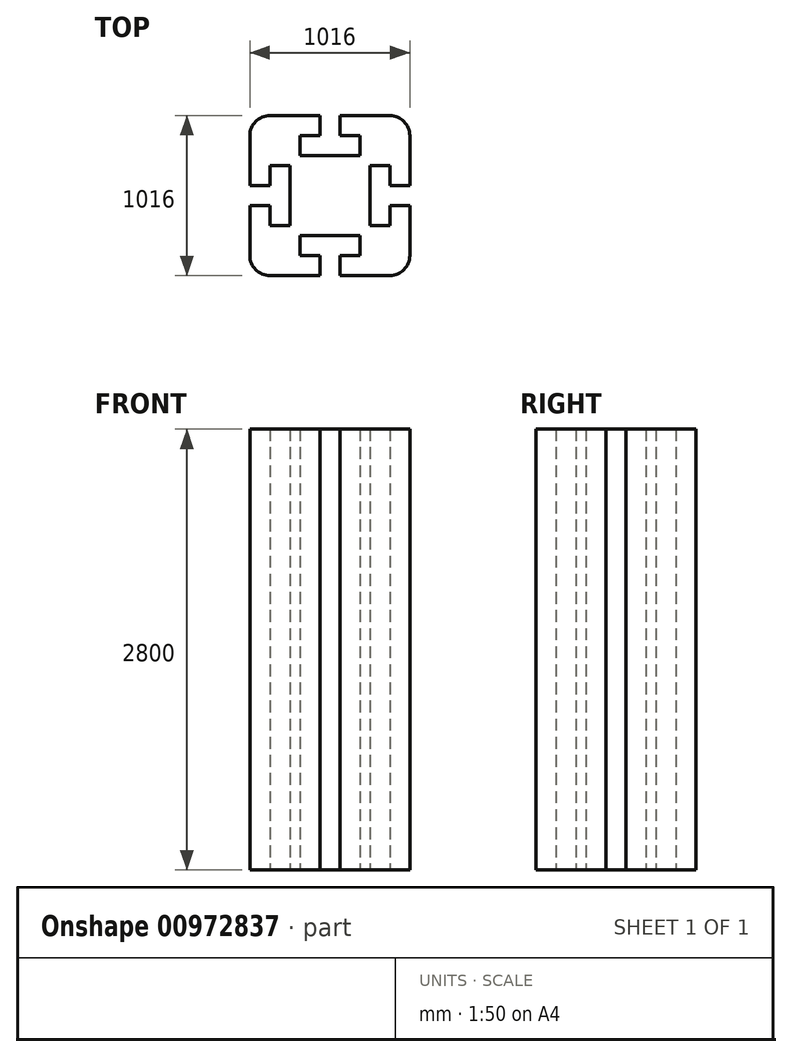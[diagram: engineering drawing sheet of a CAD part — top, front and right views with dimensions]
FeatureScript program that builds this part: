
annotation { "Feature Type Name" : "Feature", "Feature Type Description" : "" }
export const myFeature = defineFeature(function(context is Context, id is Id, definition is map)
    precondition{}
    {
        {
            var Q0;
            Q0=qCreatedBy(makeId("Top.planeOp"),FACE);
            var sketch = newSketch(context, id + "F0", { "sketchPlane" : qUnion([Q0])});
            skLineSegment(sketch, "E0.bottom", {"start": v(-381, 508) * mm, "end": v(-63.5, 508) * mm});
            skLineSegment(sketch, "E0.top", {"start": v(-381, -508) * mm, "end": v(-63.5, -508) * mm});
            skLineSegment(sketch, "E0.left", {"start": v(-508, 381) * mm, "end": v(-508, 63.5) * mm});
            skLineSegment(sketch, "E0.right", {"start": v(508, 381) * mm, "end": v(508, 63.5) * mm});
            skPoint(sketch, "E1.visualSharp", {"position": v(508, 508) * mm});
            skArc(sketch, "E1.filletArc", {"start": v(508, 381) * mm, "mid": v(470.8, 470.8) * mm, "end": v(381, 508) * mm});
            skPoint(sketch, "E2.visualSharp", {"position": v(-508, 508) * mm});
            skArc(sketch, "E2.filletArc", {"start": v(-381, 508) * mm, "mid": v(-470.8, 470.8) * mm, "end": v(-508, 381) * mm});
            skArc(sketch, "E3.filletArc", {"start": v(-508, -381) * mm, "mid": v(-470.8, -470.8) * mm, "end": v(-381, -508) * mm});
            skPoint(sketch, "E4.visualSharp", {"position": v(508, -508) * mm});
            skArc(sketch, "E4.filletArc", {"start": v(381, -508) * mm, "mid": v(470.8, -470.8) * mm, "end": v(508, -381) * mm});
            skLineSegment(sketch, "E5", {"start": v(508, 63.5) * mm, "end": v(381, 63.5) * mm});
            skLineSegment(sketch, "E6", {"start": v(381, 63.5) * mm, "end": v(381, 190.5) * mm});
            skLineSegment(sketch, "E7", {"start": v(381, 190.5) * mm, "end": v(254, 190.5) * mm});
            skLineSegment(sketch, "E8", {"start": v(254, 190.5) * mm, "end": v(254, -190.5) * mm});
            skLineSegment(sketch, "E9", {"start": v(254, -190.5) * mm, "end": v(381, -190.5) * mm});
            skLineSegment(sketch, "E10", {"start": v(381, -190.5) * mm, "end": v(381, -63.5) * mm});
            skLineSegment(sketch, "E11", {"start": v(381, -63.5) * mm, "end": v(508, -63.5) * mm});
            skLineSegment(sketch, "E12.trimOffspring", {"start": v(508, -63.5) * mm, "end": v(508, -381) * mm});
            skLineSegment(sketch, "E13", {"start": v(-508, -63.5) * mm, "end": v(-381, -63.5) * mm});
            skLineSegment(sketch, "E14", {"start": v(-381, -63.5) * mm, "end": v(-381, -190.5) * mm});
            skLineSegment(sketch, "E15", {"start": v(-381, -190.5) * mm, "end": v(-254, -190.5) * mm});
            skLineSegment(sketch, "E16", {"start": v(-254, -190.5) * mm, "end": v(-254, 190.5) * mm});
            skLineSegment(sketch, "E17", {"start": v(-254, 190.5) * mm, "end": v(-381, 190.5) * mm});
            skLineSegment(sketch, "E18", {"start": v(-381, 190.5) * mm, "end": v(-381, 63.5) * mm});
            skLineSegment(sketch, "E19", {"start": v(-381, 63.5) * mm, "end": v(-508, 63.5) * mm});
            skLineSegment(sketch, "E20", {"start": v(-63.5, -508) * mm, "end": v(-63.5, -381) * mm});
            skLineSegment(sketch, "E21", {"start": v(-63.5, -381) * mm, "end": v(-190.5, -381) * mm});
            skLineSegment(sketch, "E22", {"start": v(-190.5, -381) * mm, "end": v(-190.5, -254) * mm});
            skLineSegment(sketch, "E23", {"start": v(-190.5, -254) * mm, "end": v(190.5, -254) * mm});
            skLineSegment(sketch, "E24", {"start": v(190.5, -254) * mm, "end": v(190.5, -381) * mm});
            skLineSegment(sketch, "E25", {"start": v(190.5, -381) * mm, "end": v(63.5, -381) * mm});
            skLineSegment(sketch, "E26", {"start": v(63.5, -381) * mm, "end": v(63.5, -508) * mm});
            skPoint(sketch, "E27.orphan", {"position": v(-587.08, -63.5) * mm});
            skLineSegment(sketch, "E28.trimOffspring", {"start": v(-508, -63.5) * mm, "end": v(-508, -381) * mm});
            skLineSegment(sketch, "E29.trimOffspring", {"start": v(63.5, -508) * mm, "end": v(381, -508) * mm});
            skLineSegment(sketch, "E30", {"start": v(-63.5, 508) * mm, "end": v(-63.5, 381) * mm});
            skLineSegment(sketch, "E31", {"start": v(-63.5, 381) * mm, "end": v(-190.5, 381) * mm});
            skLineSegment(sketch, "E32", {"start": v(-190.5, 381) * mm, "end": v(-190.5, 254) * mm});
            skLineSegment(sketch, "E33", {"start": v(-190.5, 254) * mm, "end": v(190.5, 254) * mm});
            skLineSegment(sketch, "E34", {"start": v(190.5, 254) * mm, "end": v(190.5, 381) * mm});
            skLineSegment(sketch, "E35", {"start": v(190.5, 381) * mm, "end": v(63.5, 381) * mm});
            skLineSegment(sketch, "E36", {"start": v(63.5, 381) * mm, "end": v(63.5, 508) * mm});
            skPoint(sketch, "E37.orphan", {"position": v(-63.5, 575.48) * mm});
            skLineSegment(sketch, "E38.trimOffspring", {"start": v(63.5, 508) * mm, "end": v(381, 508) * mm});
            skSolve(sketch);
        }
        {
            var Q0;
            Q0=makeQuery(id+"F0.imprint","IMPRINT",FACE,{"disambiguationData":[TD([[makeQuery(id+"F0.imprint","IMPRINT",EDGE,{"derivedFrom":sQuery(id+"F0.wireOp",EDGE,"E0.bottom")}),-1.0]])]});
            extrude(context, id + "F1", {"entities" : qUnion([Q0]), "depth" : 2800 * mm, "offsetDistance" : 25.4 * mm});
        }
    });
